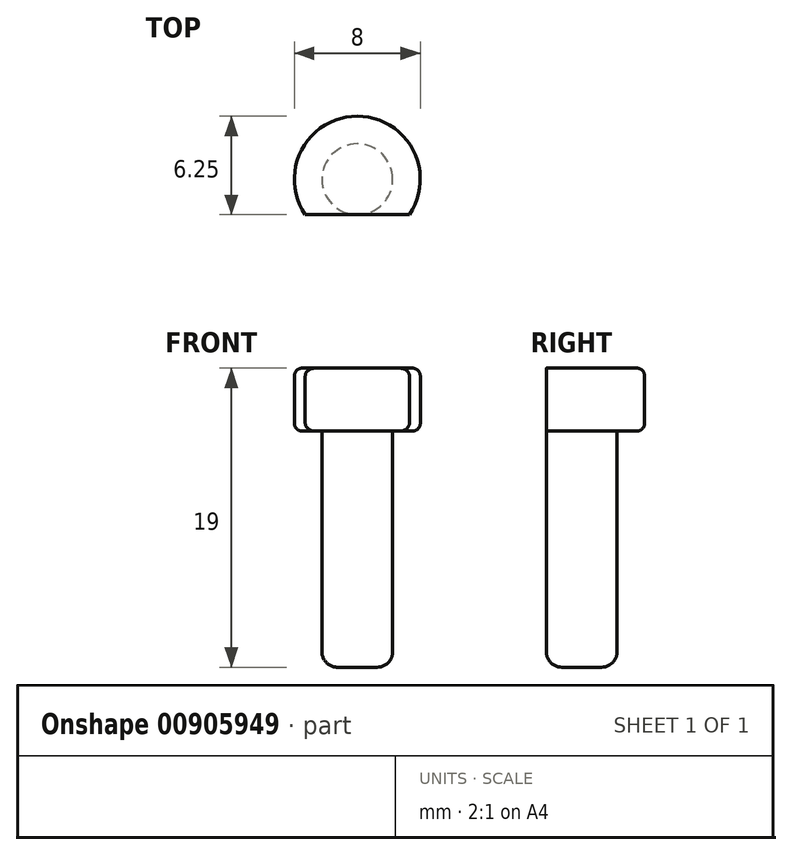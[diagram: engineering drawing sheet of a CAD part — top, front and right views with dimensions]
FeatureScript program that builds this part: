
annotation { "Feature Type Name" : "Feature", "Feature Type Description" : "" }
export const myFeature = defineFeature(function(context is Context, id is Id, definition is map)
    precondition{}
    {
        {
            var Q0;
            Q0=qCreatedBy(makeId("Top.planeOp"),FACE);
            var sketch = newSketch(context, id + "F0", { "sketchPlane" : qUnion([Q0])});
            skCircle(sketch, "E0", {"center": v(0, 0) * mm, "radius": 4 * mm});
            skSolve(sketch);
        }
        {
            var Q0;
            Q0 = qSketchRegion(id + "F0", true);
            extrude(context, id + "F1", {"entities" : qUnion([Q0]), "depth" : 4 * mm, "offsetDistance" : 25 * mm});
        }
        {
            var Q0;
            Q0=makeQuery(id+"F1.opExtrude","CAP_FACE",FACE,{"disambiguationData":[OSD([sQuery(id+"F0.wireOp",EDGE,"E0")])],"isStart":true});
            var sketch = newSketch(context, id + "F2", { "sketchPlane" : qUnion([Q0])});
            skCircle(sketch, "E1", {"center": v(0, 0) * mm, "radius": 2.25 * mm});
            skSolve(sketch);
        }
        {
            var Q0;
            Q0 = qSketchRegion(id + "F2", true);
            extrude(context, id + "F3", {"entities" : qUnion([Q0]), "operationType" : NewBodyOperationType.ADD, "depth" : 15 * mm, "offsetDistance" : 25 * mm});
        }
        {
            var Q0;
            Q0=makeQuery(id+"F1.opExtrude","CAP_FACE",FACE,{"disambiguationData":[OSD([sQuery(id+"F0.wireOp",EDGE,"E0")])],"isStart":false});
            var sketch = newSketch(context, id + "F4", { "sketchPlane" : qUnion([Q0])});
            skLineSegment(sketch, "E2", {"start": v(-4.93, -2.25) * mm, "end": v(5.11, -2.25) * mm});
            skLineSegment(sketch, "E3", {"start": v(-4.93, -2.25) * mm, "end": v(-2.24, -4.44) * mm});
            skLineSegment(sketch, "E4", {"start": v(-2.24, -4.44) * mm, "end": v(3.48, -4.44) * mm});
            skLineSegment(sketch, "E5", {"start": v(3.48, -4.44) * mm, "end": v(5.11, -2.25) * mm});
            skSolve(sketch);
        }
        {
            var Q0;
            Q0 = qSketchRegion(id + "F4", true);
            extrude(context, id + "F5", {"entities" : qUnion([Q0]), "operationType" : NewBodyOperationType.REMOVE, "oppositeDirection" : true, "depth" : 4 * mm, "offsetDistance" : 25 * mm});
        }
        {
            var Q0;
            Q0=makeQuery(id+"F3.opExtrude","CAP_EDGE",EDGE,{"disambiguationData":[OSD([sQuery(id+"F2.wireOp",EDGE,"E1")])],"isStart":false});
            fillet(context, id + "F6", {"entities" : qUnion([Q0]), "radius" : 1 * mm, "tangentPropagation" : true, "allowEdgeOverflow" : false});
        }
        {
            var Q0;
            Q0=makeQuery(id+"F1.opExtrude","CAP_EDGE",EDGE,{"disambiguationData":[OSD([sQuery(id+"F0.wireOp",EDGE,"E0")])],"isStart":true});
            var Q1;
            Q1=makeQuery(id+"F1.opExtrude","CAP_EDGE",EDGE,{"disambiguationData":[OSD([sQuery(id+"F0.wireOp",EDGE,"E0")])],"isStart":false});
            fillet(context, id + "F7", {"entities" : qUnion([Q0, Q1]), "radius" : .5 * mm, "tangentPropagation" : true, "allowEdgeOverflow" : false});
        }
    });
